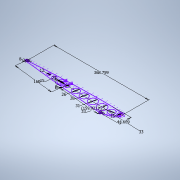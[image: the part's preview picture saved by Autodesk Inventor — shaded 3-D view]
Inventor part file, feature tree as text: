
AUTODESK INVENTOR PART (.ipt)
format: ipt  version: 2022 (Build 260153000, 153)  size: 193,536 bytes
history: native  units: mm
features: sketch x1
ambient origin geometry x8: Origin, YZ Plane, XZ Plane, XY Plane, X Axis, Y Axis, Z Axis, Center Point
feature tree (1):
  sketch  "Sketch1"  dims[d8=159.921431mm d26=5.0mm d27=5.0mm d31=34.456mm d36=5.0mm d37=5.0mm d50=368.759386mm d51=15.0mm d52=28.0mm d53=31.0mm d54=26.0mm d57=15.0mm d59=33.0mm d65=44.669323mm d66=25.0mm d67=12.0mm d68=160.0mm d69=8.0mm d70=23.0mm d71=8.0mm d73=15.0mm d77=2.0mm d78=33.0mm d79=8.0mm]
